FCSTD DOCUMENT  (FreeCAD 0.19R0.19.2)
Label: headphoneStandWithHookStudsRemovedCurrent_0
License: All rights reserved
LicenseURL: http://en.wikipedia.org/wiki/All_rights_reserved
objects: Sketcher::SketchObject×1
note: 1 computed .brp shape members not serialized (recipe doc carries the construction recipe); baked Part::Feature solids carry a one-line shape summary decoded from their .brp

FEATURE [Sketcher::SketchObject] Sketch
  FullyConstrained = false
  sketch-geometry (38):
    g0: LineSegment StartX=0 StartY=0 StartZ=0 EndX=0 EndY=100 EndZ=0
    g1: LineSegment StartX=8 StartY=65 StartZ=0 EndX=8 EndY=56 EndZ=0
    g2: Circle CenterX=8 CenterY=56 CenterZ=0 NormalX=0 NormalY=0 NormalZ=1 AngleXU=0 Radius=1
    g3: Circle CenterX=8 CenterY=52.5 CenterZ=0 NormalX=0 NormalY=0 NormalZ=1 AngleXU=0 Radius=1
    g4: Circle CenterX=11.5 CenterY=52 CenterZ=0 NormalX=0 NormalY=0 NormalZ=1 AngleXU=0 Radius=1
    g5: BSplineCurve PolesCount=3 KnotsCount=2 Degree=2 IsPeriodic=0
    g6: GeomPoint X=8 Y=56 Z=0
    g7: GeomPoint X=11.5 Y=52 Z=0
    g8: Circle CenterX=44.5 CenterY=52 CenterZ=0 NormalX=0 NormalY=0 NormalZ=1 AngleXU=0 Radius=1
    g9: Circle CenterX=48 CenterY=52.5 CenterZ=0 NormalX=0 NormalY=0 NormalZ=1 AngleXU=0 Radius=1
    g10: Circle CenterX=48 CenterY=56 CenterZ=0 NormalX=0 NormalY=0 NormalZ=1 AngleXU=0 Radius=1
    g11: BSplineCurve PolesCount=3 KnotsCount=2 Degree=2 IsPeriodic=0
    g12: GeomPoint X=44.5 Y=52 Z=0
    g13: GeomPoint X=48 Y=56 Z=0
    g14: Circle CenterX=11.5 CenterY=52 CenterZ=0 NormalX=0 NormalY=0 NormalZ=1 AngleXU=0 Radius=1
    g15: Circle CenterX=28 CenterY=49 CenterZ=0 NormalX=0 NormalY=0 NormalZ=1 AngleXU=0 Radius=1
    g16: Circle CenterX=44.5 CenterY=52 CenterZ=0 NormalX=0 NormalY=0 NormalZ=1 AngleXU=0 Radius=1
    g17: BSplineCurve PolesCount=3 KnotsCount=2 Degree=2 IsPeriodic=0
    g18: GeomPoint X=11.5 Y=52 Z=0
    g19: GeomPoint X=44.5 Y=52 Z=0
    g20: LineSegment StartX=48 StartY=65 StartZ=0 EndX=48 EndY=56 EndZ=0
    g21: LineSegment StartX=48 StartY=65 StartZ=0 EndX=56 EndY=65 EndZ=0
    g22: LineSegment StartX=56 StartY=65 StartZ=0 EndX=56 EndY=43.5 EndZ=0
    g23: Circle CenterX=56 CenterY=43.5 CenterZ=0 NormalX=0 NormalY=0 NormalZ=1 AngleXU=0 Radius=1
    g24: Circle CenterX=56 CenterY=40 CenterZ=0 NormalX=0 NormalY=0 NormalZ=1 AngleXU=0 Radius=1
    g25: Circle CenterX=52.5 CenterY=39.5 CenterZ=0 NormalX=0 NormalY=0 NormalZ=1 AngleXU=0 Radius=1
    g26: BSplineCurve PolesCount=3 KnotsCount=2 Degree=2 IsPeriodic=0
    g27: GeomPoint X=56 Y=43.5 Z=0
    g28: GeomPoint X=52.5 Y=39.5 Z=0
    g29: LineSegment StartX=0 StartY=0 StartZ=0 EndX=1 EndY=0 EndZ=0
    g30: LineSegment StartX=1 StartY=30 StartZ=0 EndX=10 EndY=30 EndZ=0
    g31: LineSegment StartX=0 StartY=100 StartZ=0 EndX=1 EndY=100 EndZ=0
    g32: Circle CenterX=8 CenterY=65 CenterZ=0 NormalX=0 NormalY=0 NormalZ=1 AngleXU=0 Radius=1
    g33: Circle CenterX=8 CenterY=81.5 CenterZ=0 NormalX=0 NormalY=0 NormalZ=1 AngleXU=0 Radius=1
    g34: Circle CenterX=1 CenterY=100 CenterZ=0 NormalX=0 NormalY=0 NormalZ=1 AngleXU=0 Radius=1
    g35: BSplineCurve PolesCount=3 KnotsCount=2 Degree=2 IsPeriodic=0
    g36: GeomPoint X=8 Y=65 Z=0
    g37: GeomPoint X=1 Y=100 Z=0
  constraints (78):
    c: Vertical(g0)
    c: Distance(g0) = 100
    c: Coincident(g0,g-1)
    c: Block(g0)
    c: Vertical(g1)
    c: Distance(g1) = 9
    c: Block(g1)
    c: Weight(g2) = 1
    c: Equal(g2,g3)
    c: Equal(g2,g4)
    c: InternalAlignment(g2,g5)
    c: InternalAlignment(g3,g5)
    c: InternalAlignment(g4,g5)
    c: InternalAlignment(g6,g5)
    c: InternalAlignment(g7,g5)
    c: Coincident(g5,g1)
    c: Block(g5)
    c: Weight(g8) = 1
    c: Equal(g8,g9)
    c: Equal(g8,g10)
    c: InternalAlignment(g8,g11)
    c: InternalAlignment(g9,g11)
    c: InternalAlignment(g10,g11)
    c: InternalAlignment(g12,g11)
    c: InternalAlignment(g13,g11)
    c: Block(g11)
    c: Weight(g14) = 1
    c: Equal(g14,g15)
    c: Equal(g14,g16)
    c: InternalAlignment(g14,g17)
    c: InternalAlignment(g15,g17)
    c: InternalAlignment(g16,g17)
    c: InternalAlignment(g18,g17)
    c: InternalAlignment(g19,g17)
    c: Coincident(g17,g5)
    c: Coincident(g17,g11)
    c: Block(g17)
    c: Vertical(g20)
    c: Coincident(g20,g11)
    c: Equal(g1,g20)
    c: Horizontal(g21)
    c: Coincident(g21,g20)
    c: Distance(g21) = 8
    c: Vertical(g22)
    c: Block(g21)
    c: Coincident(g22,g21)
    c: Distance(g22) = 21.5
    c: Weight(g23) = 1
    c: Equal(g23,g24)
    c: Equal(g23,g25)
    c: InternalAlignment(g23,g26)
    c: InternalAlignment(g24,g26)
    c: InternalAlignment(g25,g26)
    c: InternalAlignment(g27,g26)
    c: InternalAlignment(g28,g26)
    c: Coincident(g26,g22)
    c: Block(g26)
    c: Horizontal(g29)
    c: Distance(g29) = 1
    c: Coincident(g29,g0)
    c: Block(g29)
    c: Horizontal(g30)
    c: Distance(g30) = 9
    c: Horizontal(g31)
    c: Distance(g31) = 1
    c: Coincident(g31,g0)
    c: Block(g31)
    c: Weight(g32) = 1
    c: Equal(g32,g33)
    c: Equal(g32,g34)
    c: InternalAlignment(g32,g35)
    c: InternalAlignment(g33,g35)
    c: InternalAlignment(g34,g35)
    c: InternalAlignment(g36,g35)
    c: InternalAlignment(g37,g35)
    c: Coincident(g35,g31)
    c: Coincident(g35,g1)
    c: Block(g35)
